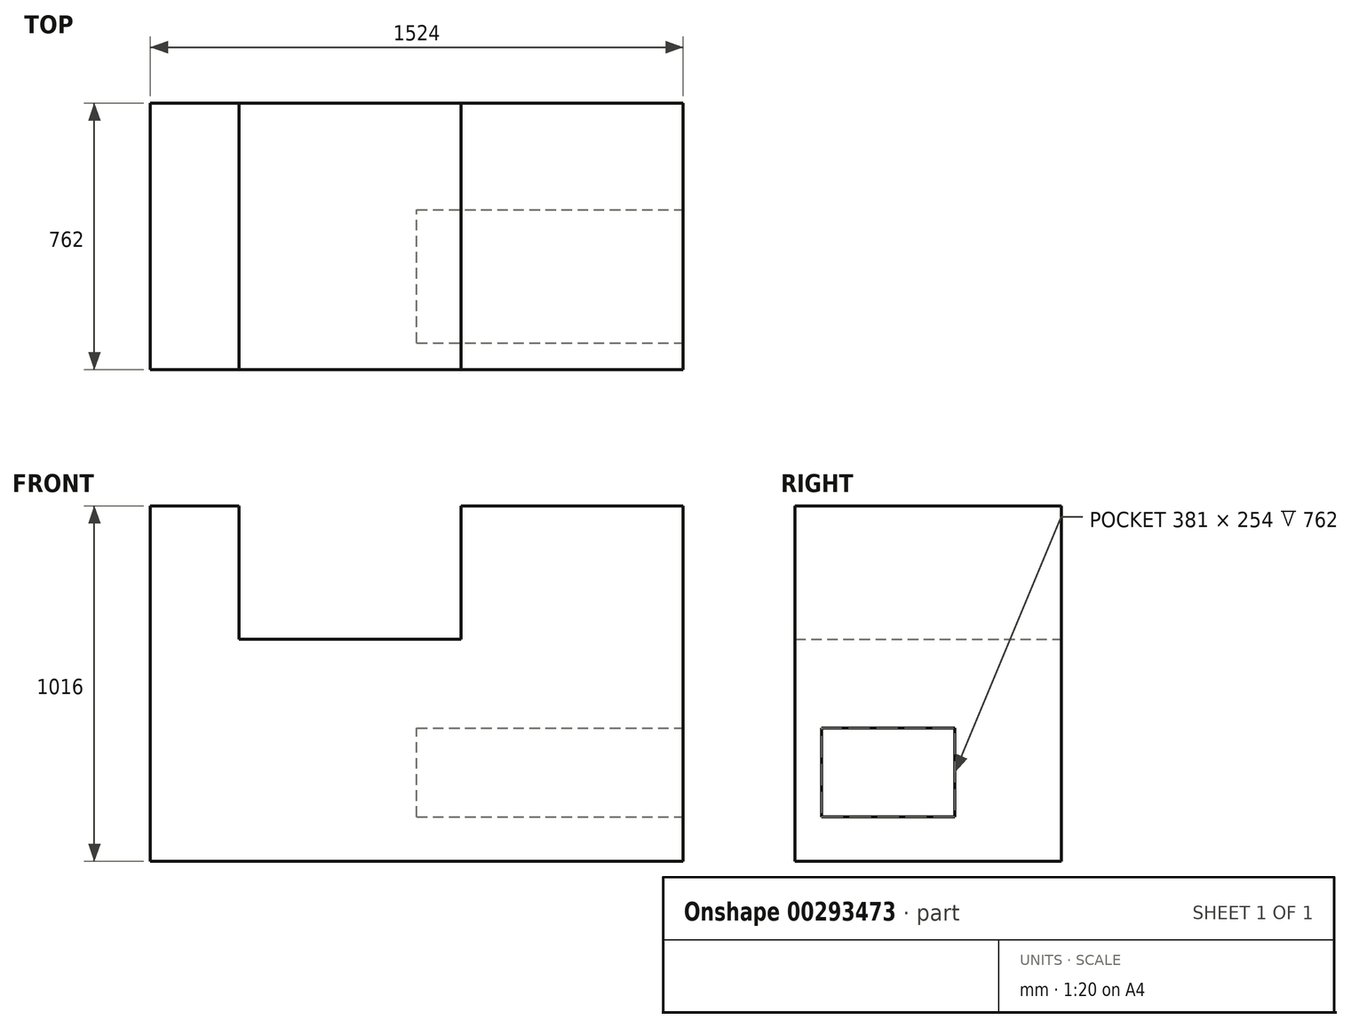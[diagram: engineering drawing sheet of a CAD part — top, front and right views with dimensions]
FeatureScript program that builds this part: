
annotation { "Feature Type Name" : "Feature", "Feature Type Description" : "" }
export const myFeature = defineFeature(function(context is Context, id is Id, definition is map)
    precondition{}
    {
        {
            var Q0;
            Q0=qCreatedBy(makeId("Front.planeOp"),FACE);
            var sketch = newSketch(context, id + "F0", { "sketchPlane" : qUnion([Q0])});
            skLineSegment(sketch, "E0.bottom", {"start": v(0, 0) * mm, "end": v(1524, 0) * mm});
            skLineSegment(sketch, "E0.left", {"start": v(0, 0) * mm, "end": v(0, 1016) * mm});
            skLineSegment(sketch, "E0.right", {"start": v(1524, 0) * mm, "end": v(1524, 1016) * mm});
            skLineSegment(sketch, "E1", {"start": v(0, 1016) * mm, "end": v(254, 1016) * mm});
            skLineSegment(sketch, "E2.top", {"start": v(254, 635) * mm, "end": v(889, 635) * mm});
            skLineSegment(sketch, "E2.left", {"start": v(254, 1016) * mm, "end": v(254, 635) * mm});
            skLineSegment(sketch, "E2.right", {"start": v(889, 1016) * mm, "end": v(889, 635) * mm});
            skLineSegment(sketch, "E3", {"start": v(889, 1016) * mm, "end": v(1524, 1016) * mm});
            skSolve(sketch);
        }
        {
            var Q0;
            Q0 = qSketchRegion(id + "F0", true);
            extrude(context, id + "F1", {"entities" : qUnion([Q0]), "depth" : 762 * mm});
        }
        {
            var Q0;
            Q0=makeQuery(id+"F1.opExtrude","SWEPT_FACE",FACE,{"disambiguationData":[OSD([sQuery(id+"F0.wireOp",EDGE,"E0.right")])]});
            var sketch = newSketch(context, id + "F2", { "sketchPlane" : qUnion([Q0])});
            skLineSegment(sketch, "E4", {"start": v(-762, 0) * mm, "end": v(-762, 127) * mm});
            skLineSegment(sketch, "E5", {"start": v(-762, 127) * mm, "end": v(-685.8, 127) * mm});
            skLineSegment(sketch, "E6.bottom", {"start": v(-685.8, 127) * mm, "end": v(-304.8, 127) * mm});
            skLineSegment(sketch, "E6.top", {"start": v(-685.8, 381) * mm, "end": v(-304.8, 381) * mm});
            skLineSegment(sketch, "E6.left", {"start": v(-685.8, 127) * mm, "end": v(-685.8, 381) * mm});
            skLineSegment(sketch, "E6.right", {"start": v(-304.8, 127) * mm, "end": v(-304.8, 381) * mm});
            skSolve(sketch);
        }
        {
            var Q0;
            Q0=makeQuery(id+"F2.imprint","IMPRINT",FACE,{"disambiguationData":[TD([[makeQuery(id+"F2.imprint","IMPRINT",EDGE,{"derivedFrom":sQuery(id+"F2.wireOp",EDGE,"E6.bottom")}),1.0]])]});
            extrude(context, id + "F3", {"entities" : qUnion([Q0]), "operationType" : NewBodyOperationType.REMOVE, "oppositeDirection" : true, "depth" : 762 * mm});
        }
    });
